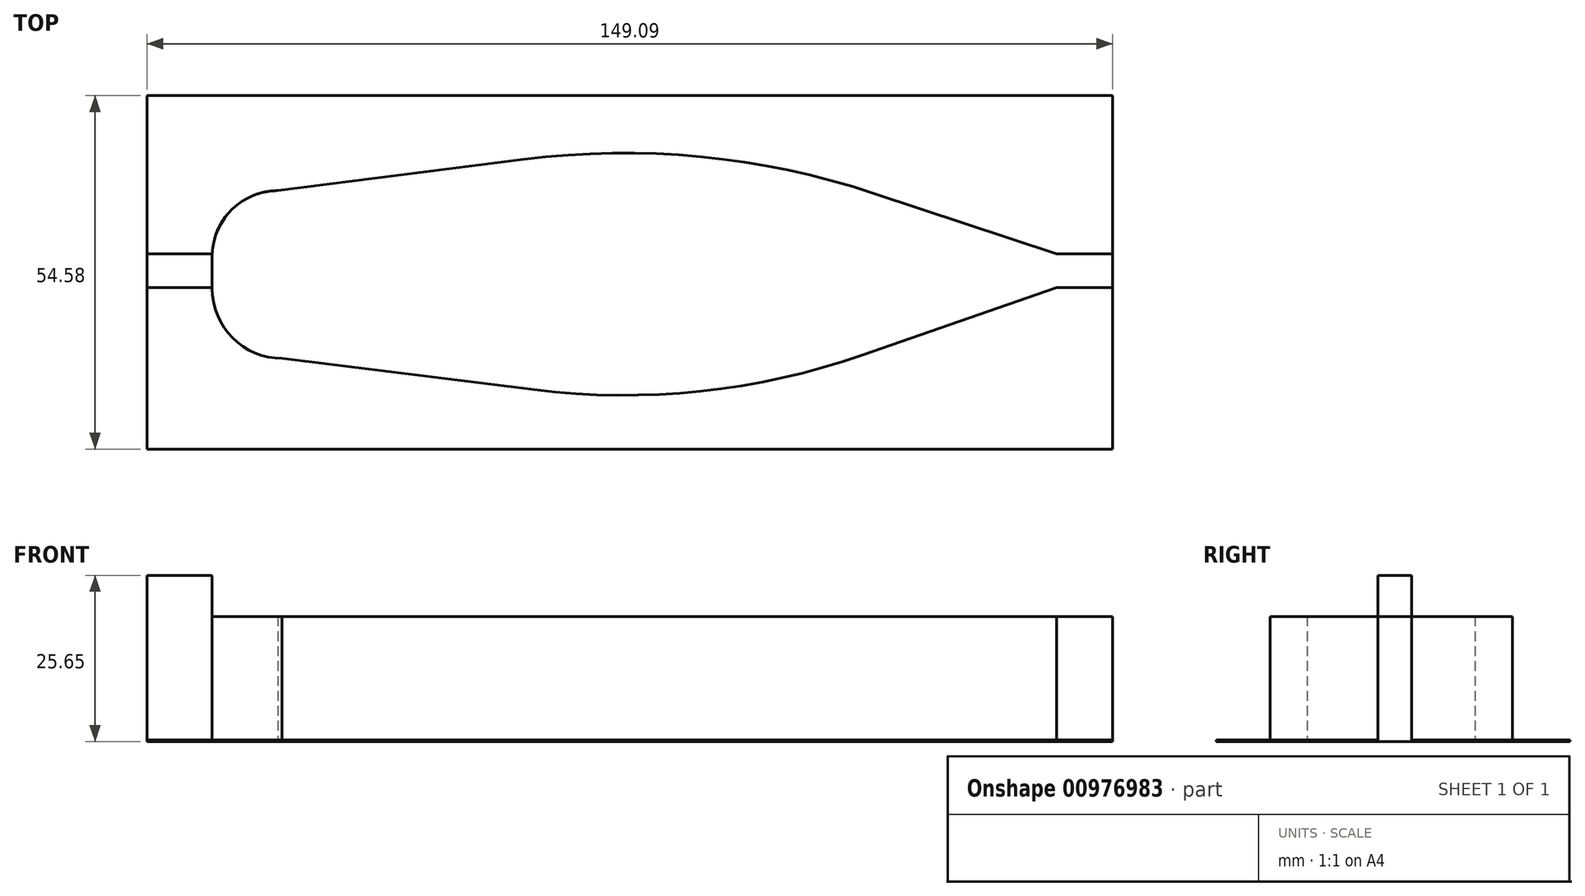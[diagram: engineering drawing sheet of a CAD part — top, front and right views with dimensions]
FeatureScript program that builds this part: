
annotation { "Feature Type Name" : "Feature", "Feature Type Description" : "" }
export const myFeature = defineFeature(function(context is Context, id is Id, definition is map)
    precondition{}
    {
        {
            var Q0;
            Q0=qCreatedBy(makeId("Top.planeOp"),FACE);
            var sketch = newSketch(context, id + "F0", { "sketchPlane" : qUnion([Q0])});
            skLineSegment(sketch, "E0.bottom", {"start": v(-74.69, 0) * mm, "end": v(74.4, 0) * mm});
            skLineSegment(sketch, "E0.top", {"start": v(-74.69, 54.58) * mm, "end": v(74.4, 54.58) * mm});
            skLineSegment(sketch, "E0.left", {"start": v(-74.69, 0) * mm, "end": v(-74.69, 54.58) * mm});
            skLineSegment(sketch, "E0.right", {"start": v(74.4, 0) * mm, "end": v(74.4, 54.58) * mm});
            skSolve(sketch);
        }
        {
            var Q0;
            Q0=makeQuery(id+"F0.imprint","IMPRINT",FACE,{"disambiguationData":[TD([[makeQuery(id+"F0.imprint","IMPRINT",EDGE,{"derivedFrom":sQuery(id+"F0.wireOp",EDGE,"E0.bottom")}),1.0]])]});
            extrude(context, id + "F1", {"entities" : qUnion([Q0]), "depth" : 0.25 * mm, "offsetDistance" : 25.4 * mm});
        }
        {
            var Q0;
            Q0=makeQuery(id+"F1.opExtrude","CAP_FACE",FACE,{"disambiguationData":[OSD([sQuery(id+"F0.wireOp",EDGE,"E0.bottom"),sQuery(id+"F0.wireOp",EDGE,"E0.top"),sQuery(id+"F0.wireOp",EDGE,"E0.left"),sQuery(id+"F0.wireOp",EDGE,"E0.right")])],"isStart":false});
            var sketch = newSketch(context, id + "F2", { "sketchPlane" : qUnion([Q0])});
            skLineSegment(sketch, "E1.bottom", {"start": v(-74.69, 30.12) * mm, "end": v(-64.61, 30.12) * mm});
            skLineSegment(sketch, "E1.top", {"start": v(-74.69, 24.94) * mm, "end": v(-64.61, 24.94) * mm});
            skLineSegment(sketch, "E1.left", {"start": v(-74.69, 30.12) * mm, "end": v(-74.69, 24.94) * mm});
            skLineSegment(sketch, "E1.right", {"start": v(-64.61, 30.12) * mm, "end": v(-64.61, 24.94) * mm});
            skSolve(sketch);
        }
        {
            var Q0;
            Q0 = qSketchRegion(id + "F2", true);
            extrude(context, id + "F3", {"entities" : qUnion([Q0]), "operationType" : NewBodyOperationType.ADD, "depth" : 25.4 * mm, "offsetDistance" : 25.4 * mm});
        }
        {
            var Q0;
            Q0=makeQuery(id+"F1.opExtrude","CAP_FACE",FACE,{"disambiguationData":[OSD([sQuery(id+"F0.wireOp",EDGE,"E0.bottom"),sQuery(id+"F0.wireOp",EDGE,"E0.top"),sQuery(id+"F0.wireOp",EDGE,"E0.left"),sQuery(id+"F0.wireOp",EDGE,"E0.right")])],"isStart":false});
            var sketch = newSketch(context, id + "F4", { "sketchPlane" : qUnion([Q0])});
            skLineSegment(sketch, "E2.left", {"start": v(-64.61, 29.74) * mm, "end": v(-64.61, 24.81) * mm});
            skPoint(sketch, "E3.visualSharp", {"position": v(-64.61, 14) * mm});
            skArc(sketch, "E3.filletArc", {"start": v(-64.61, 24.81) * mm, "mid": v(-61.45, 17.17) * mm, "end": v(-53.8, 14) * mm});
            skPoint(sketch, "E4.visualSharp", {"position": v(-64.61, 39.9) * mm});
            skArc(sketch, "E4.filletArc", {"start": v(-54.44, 39.9) * mm, "mid": v(-61.63, 36.93) * mm, "end": v(-64.61, 29.74) * mm});
            skLineSegment(sketch, "E5.bottom", {"start": v(74.4, 30.12) * mm, "end": v(65.76, 30.12) * mm});
            skLineSegment(sketch, "E5.top", {"start": v(74.4, 24.94) * mm, "end": v(65.76, 24.94) * mm});
            skLineSegment(sketch, "E5.left", {"start": v(74.4, 30.12) * mm, "end": v(74.4, 24.94) * mm});
            skLineSegment(sketch, "E6", {"start": v(-54.44, 39.9) * mm, "end": v(-16.52, 44.74) * mm});
            skLineSegment(sketch, "E7", {"start": v(37.5, 39.5) * mm, "end": v(65.76, 30.12) * mm});
            skLineSegment(sketch, "E8", {"start": v(-53.8, 14) * mm, "end": v(-14.88, 9.17) * mm});
            skLineSegment(sketch, "E9", {"start": v(35.8, 14.53) * mm, "end": v(65.76, 24.94) * mm});
            skPoint(sketch, "E10.visualSharp", {"position": v(11.08, 5.95) * mm});
            skArc(sketch, "E10.filletArc", {"start": v(-14.88, 9.17) * mm, "mid": v(10.76, 8.94) * mm, "end": v(35.8, 14.53) * mm});
            skPoint(sketch, "E11.visualSharp", {"position": v(11.08, 48.25) * mm});
            skArc(sketch, "E11.filletArc", {"start": v(37.5, 39.5) * mm, "mid": v(10.78, 45.15) * mm, "end": v(-16.52, 44.74) * mm});
            skSolve(sketch);
        }
        {
            var Q0;
            {var subQ3=sQuery(id+"F4.wireOp",EDGE,"E3.filletArc");Q0=makeQuery(id+"F4.imprint","IMPRINT",FACE,{"disambiguationData":[TD([[makeQuery(id+"F4.imprint","IMPRINT",EDGE,{"derivedFrom":subQ3}),1.0]])]});}
            extrude(context, id + "F5", {"entities" : qUnion([Q0]), "operationType" : NewBodyOperationType.ADD, "depth" : 19.05 * mm, "offsetDistance" : 25.4 * mm});
        }
        {
            var Q0;
            Q0=makeQuery(id+"F5.opExtrude","CAP_FACE",FACE,{"disambiguationData":[OSD([sQuery(id+"F4.wireOp",EDGE,"E2.left"),sQuery(id+"F4.wireOp",EDGE,"E3.filletArc"),sQuery(id+"F4.wireOp",EDGE,"E4.filletArc"),sQuery(id+"F4.wireOp",EDGE,"E5.bottom"),sQuery(id+"F4.wireOp",EDGE,"E5.top"),sQuery(id+"F4.wireOp",EDGE,"E5.left"),sQuery(id+"F4.wireOp",EDGE,"E6"),sQuery(id+"F4.wireOp",EDGE,"E7"),sQuery(id+"F4.wireOp",EDGE,"E8"),sQuery(id+"F4.wireOp",EDGE,"E9"),sQuery(id+"F4.wireOp",EDGE,"E10.filletArc"),sQuery(id+"F4.wireOp",EDGE,"E11.filletArc")])],"isStart":false});
            var sketch = newSketch(context, id + "F6", { "sketchPlane" : qUnion([Q0])});
            skPoint(sketch, "E12.firstSnap0", {"position": v(-61.5, 37.06) * mm});
            skLineSegment(sketch, "E12.bottom", {"start": v(-56.4, 37.06) * mm, "end": v(-53.8, 37.06) * mm});
            skLineSegment(sketch, "E12.top", {"start": v(-56.4, 16.84) * mm, "end": v(-53.8, 16.84) * mm});
            skLineSegment(sketch, "E12.left", {"start": v(-56.4, 37.06) * mm, "end": v(-56.4, 16.84) * mm});
            skLineSegment(sketch, "E13", {"start": v(37.69, 36.8) * mm, "end": v(37.69, 17.77) * mm});
            skLineSegment(sketch, "E14", {"start": v(37.69, 36.8) * mm, "end": v(6.69, 40.95) * mm});
            skLineSegment(sketch, "E15", {"start": v(37.69, 17.77) * mm, "end": v(7.86, 13.37) * mm});
            skLineSegment(sketch, "E16", {"start": v(-53.8, 37.06) * mm, "end": v(-6.72, 41.25) * mm});
            skLineSegment(sketch, "E17", {"start": v(-53.8, 16.84) * mm, "end": v(-7.92, 12.89) * mm});
            skPoint(sketch, "E18.visualSharp", {"position": v(0, 12.2) * mm});
            skArc(sketch, "E18.filletArc", {"start": v(-7.92, 12.89) * mm, "mid": v(-0.01, 12.67) * mm, "end": v(7.86, 13.37) * mm});
            skPoint(sketch, "E19.visualSharp", {"position": v(0, 41.85) * mm});
            skArc(sketch, "E19.filletArc", {"start": v(6.69, 40.95) * mm, "mid": v(0, 41.47) * mm, "end": v(-6.72, 41.25) * mm});
            skSolve(sketch);
        }
        {
            var Q0;
            Q0=makeQuery(id+"F6.imprint","IMPRINT",FACE,{"disambiguationData":[TD([[makeQuery(id+"F6.imprint","IMPRINT",EDGE,{"derivedFrom":sQuery(id+"F6.wireOp",EDGE,"E12.bottom")}),-1.0]])]});
            extrude(context, id + "F7", {"entities" : qUnion([Q0]), "operationType" : NewBodyOperationType.ADD, "oppositeDirection" : true, "depth" : 12.7 * mm, "offsetDistance" : 25.4 * mm});
        }
    });
